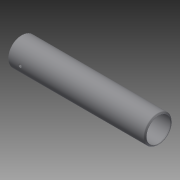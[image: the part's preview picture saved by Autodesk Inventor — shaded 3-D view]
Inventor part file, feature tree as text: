
AUTODESK INVENTOR PART (.ipt)
format: ipt  version: 2014 SP2 (Build 180246200, 246)  size: 150,016 bytes
history: native  units: in
note: dims shown in document units (in); Inventor stores cm internally (conversion verified against a paired STEP export)
features: other x42, sketch x2, revolve x1, extrude x1
ambient origin geometry x8: Origin, YZ Plane, XZ Plane, XY Plane, X Axis, Y Axis, Z Axis, Center Point
bodies: Solid1 (feature_tree)
feature tree (46):
  revolve  "Revolution1"  [1 undecoded]
  extrude  "Extrusion1"  [1 undecoded]
  other  "cp1_XY"
  other  "cp1_YZ"
  other  "cp1_ZX"
  other  "cp1_X"
  other  "cp1_Y"
  other  "cp1_Z"
  other  "cp1_Center"
  other  "cp2_XY"
  other  "cp2_YZ"
  other  "cp2_ZX"
  other  "cp2_X"
  other  "cp2_Y"
  other  "cp2_Z"
  other  "cp2_Center"
  other  "cp3_XY"
  other  "cp3_YZ"
  other  "cp3_ZX"
  other  "cp3_X"
  other  "cp3_Y"
  other  "cp3_Z"
  other  "cp3_Center"
  other  "cp4_XY"
  other  "cp4_YZ"
  other  "cp4_ZX"
  other  "cp4_X"
  other  "cp4_Y"
  other  "cp4_Z"
  other  "cp4_Center"
  other  "tube_front_XY"
  other  "tube_front_YZ"
  other  "tube_front_ZX"
  other  "tube_front_X"
  other  "tube_front_Y"
  other  "tube_front_Z"
  other  "tube_front_Center"
  other  "tube_rear_XY"
  other  "tube_rear_YZ"
  other  "tube_rear_ZX"
  other  "tube_rear_X"
  other  "tube_rear_Y"
  other  "tube_rear_Z"
  other  "tube_rear_Center"
  sketch  "Sketch_1"  dims[d0=360.0deg d1=0.4025in d2=0.0in]
  sketch  "Sketch_4"
note: 2 required parameter values undecoded (feature->parameter linkage not recoverable at this tier; creation-order binding heuristic only, values carry confidence <= 0.55)